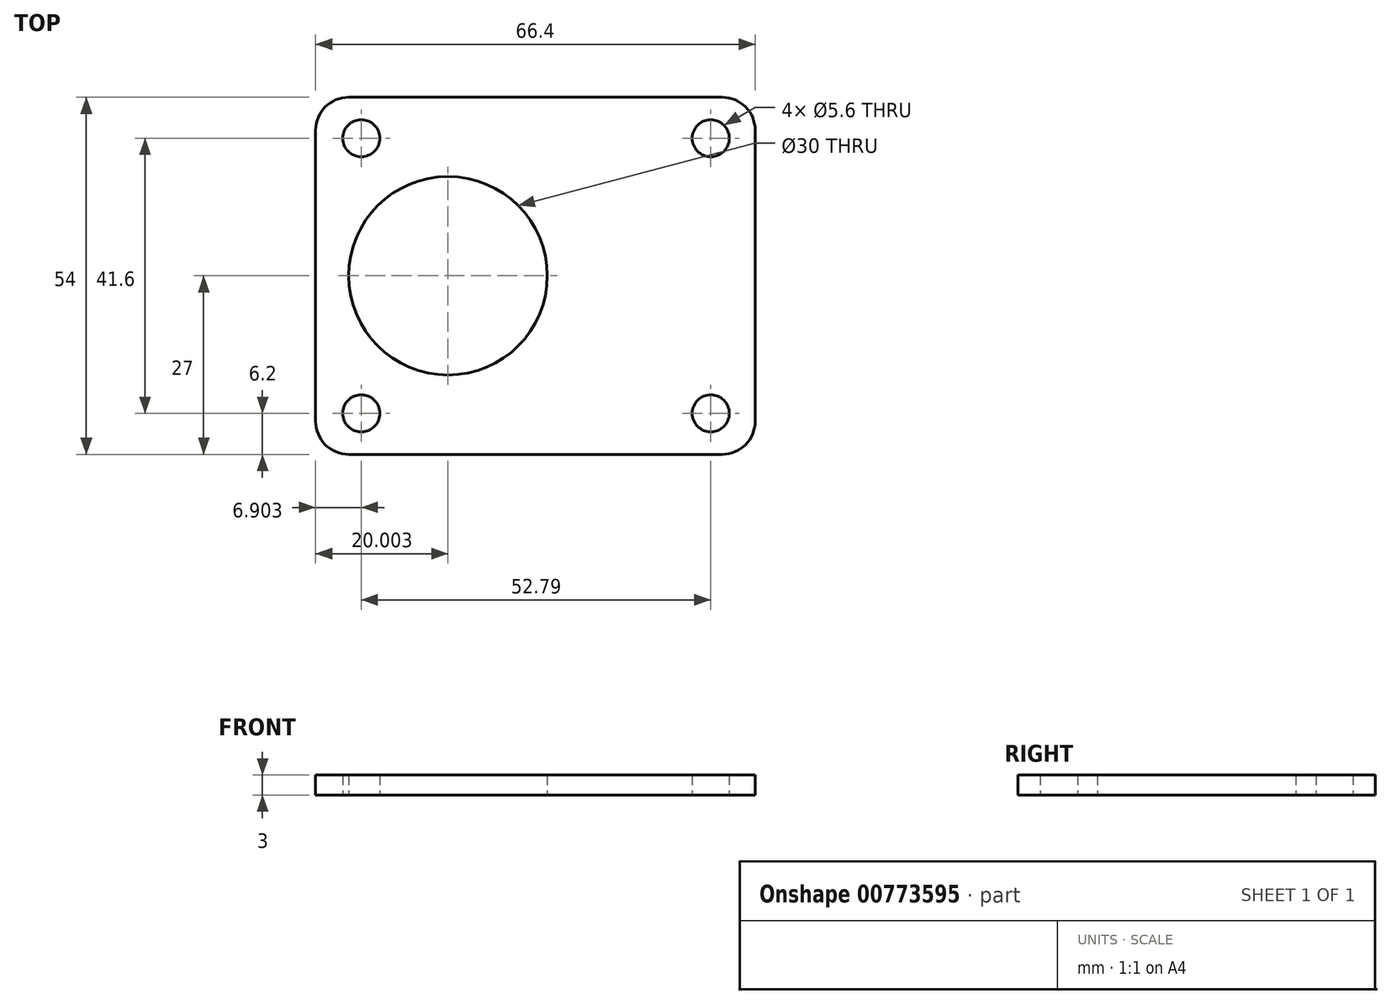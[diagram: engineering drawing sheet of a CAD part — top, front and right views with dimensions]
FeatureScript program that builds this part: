
annotation { "Feature Type Name" : "Feature", "Feature Type Description" : "" }
export const myFeature = defineFeature(function(context is Context, id is Id, definition is map)
    precondition{}
    {
        {
            var Q0;
            Q0=qCreatedBy(makeId("Top.planeOp"), FACE);
            var sketch = newSketch(context, id + "F0", { "sketchPlane" : qUnion([Q0])});
            skLineSegment(sketch, "E0.left", {"start": v(-36.4, 22) * mm, "end": v(-36.4, -22) * mm});
            skCircle(sketch, "E1", {"center": v(-29.5, 20.8) * mm, "radius": 2.8 * mm});
            skLineSegment(sketch, "E2", {"start": v(-29.5, -27) * mm, "end": v(-29.5, -20.8) * mm});
            skCircle(sketch, "E3", {"center": v(23.28, 20.8) * mm, "radius": 2.8 * mm});
            skCircle(sketch, "E4", {"center": v(-29.5, -20.8) * mm, "radius": 2.8 * mm});
            skCircle(sketch, "E5", {"center": v(23.28, -20.8) * mm, "radius": 2.8 * mm});
            skPoint(sketch, "E6.visualSharp", {"position": v(-36.4, 27) * mm});
            skArc(sketch, "E6.filletArc", {"start": v(-31.4, 27) * mm, "mid": v(-34.94, 25.54) * mm, "end": v(-36.4, 22) * mm});
            skPoint(sketch, "E7.visualSharp", {"position": v(-36.4, -27) * mm});
            skArc(sketch, "E7.filletArc", {"start": v(-36.4, -22) * mm, "mid": v(-34.94, -25.54) * mm, "end": v(-31.4, -27) * mm});
            skLineSegment(sketch, "E8", {"start": v(14.62, -11.38) * mm, "end": v(14.62, -11.38) * mm});
            skLineSegment(sketch, "E9", {"start": v(-31.4, 27) * mm, "end": v(25, 27) * mm});
            skLineSegment(sketch, "E10", {"start": v(-31.4, -27) * mm, "end": v(25, -27) * mm});
            skLineSegment(sketch, "E11", {"start": v(30, 22) * mm, "end": v(30, -22) * mm});
            skPoint(sketch, "E12.visualSharp", {"position": v(30, 27) * mm});
            skArc(sketch, "E12.filletArc", {"start": v(30, 22) * mm, "mid": v(28.53, 25.54) * mm, "end": v(25, 27) * mm});
            skPoint(sketch, "E13.visualSharp", {"position": v(30, -27) * mm});
            skArc(sketch, "E13.filletArc", {"start": v(25, -27) * mm, "mid": v(28.53, -25.54) * mm, "end": v(30, -22) * mm});
            skCircle(sketch, "E14", {"center": v(-16.4, 0) * mm, "radius": 15 * mm});
            skSolve(sketch);
        }
        {
            var Q0;
            Q0 = qSketchRegion(id + "F0", true);
            extrude(context, id + "F1", {"entities" : qUnion([Q0]), "depth" : 3 * mm, "offsetDistance" : 25 * mm});
        }
    });
